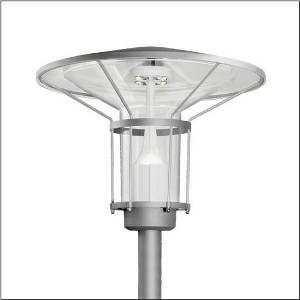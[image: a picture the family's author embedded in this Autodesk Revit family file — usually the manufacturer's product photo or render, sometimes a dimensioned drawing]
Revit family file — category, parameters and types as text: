
# Revit family: laterne_classic_iq___st1_2a_5xa5245kf14h_95b8
name_source: partatom
category: Lighting Fixtures
units: mm (PartAtom-declared; Revit-internal decimal feet)

## family parameters
Cut with Voids When Loaded = No
Host = Face
Light Source = No
Part Type = Normal
Room Calculation Point = No
Round Connector Dimension = Use Diameter
Shared = No

## types (1)
- --- (1 x LED, 1380 lm, 10 W, 4000K)
    Apparent Load = 10 VA
    CIE Flux Codes = 21 60 93 97 100
    Color Rendering = 70
    Color Temperature = 4000K
    Default Elevation = 1800 mm
    Description = Lantern Classic iQ, mast luminaire, Module 540 iQ-SR, primary light control with 3 zone facetted reflector, of plastic, silver coated, highly specular, structured, primary optical cover: cover, of PMMA, transparent, light distribution: ST1.2a, light emission: direct distribution, primary light characteristic: asymmetric, installation type: post-top, LED, High Power LED, rated luminous flux: 1.380lm, luminous efficacy: 138lm/W, light colour: 740, colour temperature: 4000K, control gear: ECG iQ, control: presetting dimming logarithmic, Street-Remote, Auto-Match, Temp-Guard, Lumen-Switch, Night-Set, Smart-Wire, Light-Fading, Desk-Remote (wireless, voltage-free reading and setting of iQ features in the workshop via application-optimized NFC function/RFID function), optimised constant luminous flux control (CLO 2.0), with terminal, 6-pole, max. 2.5mm², mains connection: 220..240V, AC, 50/60Hz, start of lifetime: 10W, end of lifetime: 10W, reduction: 5W, luminaire housing, upper part, of glass-fibre reinforced polyester, coated, Siteco® metallic grey (DB 702S), diameter: 750mm, height: 596mm, spigot size: d x l = 76 x 70mm (post-top) | with reducer (optional accessory) 60 x 70mm, post-top mast mounting element, of diecast aluminium, coated, Siteco® metallic grey (DB 702S), Module 540 iQ-SR, traffic white (RAL 9016), equipment: standard, protection rating (complete): IP65, insulation class (complete): insulation class II (safety insulation), certification: CE, ENEC, VDE, packaging unit: 1 piece

Light Distribution: ST1.2a
    Height = 596 mm
    Lamp = 1 x LED
    Lamp Light Flux = 1380 lm
    Lamp Power = 10 W
    Lamp count = 1
    Length = 750 mm
    Luminous efficacy = 138 lm/W
    Manufacturer = Siteco
    ModVariant = No
    Model = 5XA5245KF14H
    Number of Poles = 1
    OnlyDefault = Yes
    Power Factor = 1
    Product Name = Laterne Classic iQ | ST1.2a
    Product group = mast luminaire | pylon top
    ProductGroupID = 6100
    Protection Class = Protection class II
    Protection Degree = IP 65
    RLX_Detail_Level = 1
    RlxData = <blob elided: 95777 chars, md5=4b6434a3>
    Socket = socket
    Standby Power = 0 W
    System Light Flux = 1380 lm
    System Power = 10 W
    Type Comments = factory setting: luminous flux: 100 % | dim-lin: 254 | 401 mA
    Type Image = l_1006052.jpg
    URL = http://relux.com
    VarID = @adj_071589
    Voltage = 0 V
    Weight = 0.00 kg
    Width = 0 mm  [stored 0 ft]

note: [stored X ft] marks values corroborated as IEEE doubles in the binary element streams (Revit-internal decimal feet)

## geometry (parser evidence)
native form markers: Blend x4, Sweep x10
no freeform markers — native parametric forms only
